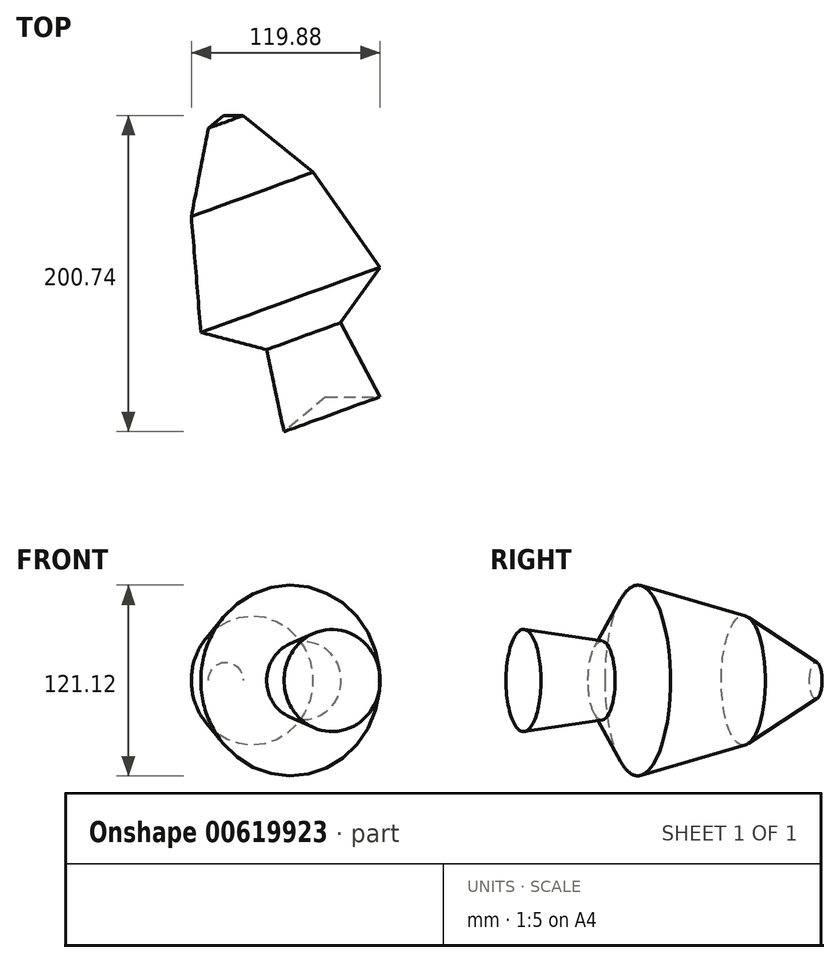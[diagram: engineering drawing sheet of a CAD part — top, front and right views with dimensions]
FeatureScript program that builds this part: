
annotation { "Feature Type Name" : "Feature", "Feature Type Description" : "" }
export const myFeature = defineFeature(function(context is Context, id is Id, definition is map)
    precondition{}
    {
        {
            var Q0;
            Q0=qCreatedBy(makeId("Top.planeOp"),FACE);
            var sketch = newSketch(context, id + "F0", { "sketchPlane" : qUnion([Q0])});
            skLineSegment(sketch, "E0", {"start": v(0, 0) * mm, "end": v(34.53, 0) * mm});
            skLineSegment(sketch, "E1", {"start": v(34.53, 0) * mm, "end": v(9.52, 47.07) * mm});
            skLineSegment(sketch, "E2", {"start": v(9.52, 47.07) * mm, "end": v(34.53, 82.23) * mm});
            skLineSegment(sketch, "E3", {"start": v(34.53, 82.23) * mm, "end": v(-8.16, 142.59) * mm});
            skLineSegment(sketch, "E4", {"start": v(-8.16, 142.59) * mm, "end": v(-52.54, 178.56) * mm});
            skLineSegment(sketch, "E5", {"start": v(-52.54, 178.56) * mm, "end": v(-64.94, 178.56) * mm});
            skLineSegment(sketch, "E6", {"start": v(-64.94, 178.56) * mm, "end": v(0, 0) * mm});
            skSolve(sketch);
        }
        {
            var Q0;
            Q0=makeQuery(id+"F0.imprint","IMPRINT",FACE,{"disambiguationData":[TD([[makeQuery(id+"F0.imprint","IMPRINT",EDGE,{"derivedFrom":sQuery(id+"F0.wireOp",EDGE,"E0")}),1.0]])]});
            var Q1;
            Q1=sQuery(id+"F0.wireOp",EDGE,"E6");
            revolve(context, id + "F1", {"entities" : qUnion([Q0]), "axis" : qUnion([Q1]), "revolveType" : RevolveType.FULL});
        }
    });
